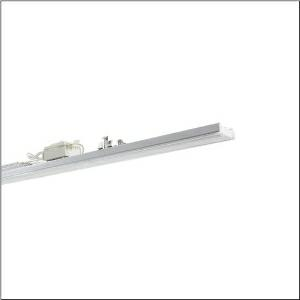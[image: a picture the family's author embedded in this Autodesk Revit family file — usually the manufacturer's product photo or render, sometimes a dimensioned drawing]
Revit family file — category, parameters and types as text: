
# Revit family: licross_11_recessed_extreme_mo_51tl12dv4fxge
name_source: partatom
category: Lighting Fixtures
units: mm (PartAtom-declared; Revit-internal decimal feet)

## family parameters
Cut with Voids When Loaded = No
Host = Face
Light Source = No
Part Type = Normal
Room Calculation Point = No
Round Connector Dimension = Use Diameter
Shared = No

## types (1)
- --- (1 x LED, 15360 lm, 84.1 W, 4000K)
    Apparent Load = 84 VA
    CIE Flux Codes = 67 92 99 100 100
    Color Rendering = 80
    Color Temperature = 4000K
    Default Elevation = 1800 mm
    Description = Licross 11 Recessed extreme MO, luminaire insert, of sheet steel, coil coated, white, length: 2.250mm, width: 66mm, height: 67mm, LED rated luminous flux: 15.360lm, light colour: 840, SDCM (Standard Deviation of Colour Matching)MacAdam ≤ 2 SDCM (initial), control gear: DALI 2, with plug, 5-pole, with phase selection, mains connection: 220..240V, AC, 50/60Hz, rated input power: 84W, internal wiring halogen-free, primary optical cover: cover, of PMMA, light emission: direct distribution, primary light characteristic: symmetric, protection rating (complete): IP40, insulation class (complete): insulation class I (protective earthing), certification: CE, ENEC, VDE, UKCA, protection symbol: D if used in an environment without relevant dust loads with corresponding accessories, impact resistance: IK06, permissible ambient temperature for indoor applications: -40..+45°C, corresponds to IFS (International Featured Standards) requirements for safety and quality in the food industry, reducing of maximum allowable ambient temperature of 5°C with ceiling mounting, LABS conformity tested according to VDMA 24364:2018-05, The light source and the operating device comply with the requirements of the Ecodesign Regulation (EU) 2019/2020 and are replaceable in accordance with this regulation, packaging unit: 1 piece
    Height = 58 mm
    Lamp = 1 x LED
    Lamp Light Flux = 15360 lm
    Lamp Power = 84.1 W
    Lamp count = 1
    Length = 2250 mm
    Luminous efficacy = 183 lm/W
    Manufacturer = Siteco
    ModVariant = No
    Model = 51TL12DV4FXGE
    Mounting Place = Ceiling
    Mounting Type = Pendant
    Number of Poles = 1
    OnlyDefault = Yes
    Power Factor = 1
    Product Name = Licross 11 Recessed extreme MO
    Product group = luminaire insert | ceiling pendant
    ProductGroupID = 901
    Protection Class = Protection class I
    Protection Degree = IP 40
    RLX_Detail_Level = 1
    RLX_Emergency_Light_Flux = 0 lm
    RLX_Emergency_Type = 0
    RLX_Emergency_Type_DB = No
    RlxData = <blob elided: 29753 chars, md5=124ef79e>
    Socket = socket
    Standby Power = 0 W
    System Light Flux = 15360 lm
    System Power = 84 W
    Type Comments = factory setting: luminous flux: 100 % | dim-lin: 254 | 378 mA
    Type Image = l_1296930.jpg
    URL = http://relux.com
    VarID = @adj_087533
    Voltage = 0 V
    Weight = 0.00 kg
    Width = 66 mm

## geometry (parser evidence)
native form markers: Blend x4, Sweep x10
no freeform markers — native parametric forms only
